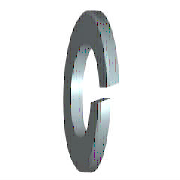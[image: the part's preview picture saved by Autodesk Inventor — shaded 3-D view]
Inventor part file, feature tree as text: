
AUTODESK INVENTOR PART (.ipt)
format: ipt  version: 2024 (Build 280153000, 153)  size: 125,440 bytes
history: native  units: mm (DEFAULTED — no unit token found)
features: extrude x2, other x1, plane x1
ambient origin geometry x6: Origin, YZ Plane, X Axis, Y Axis, Z Axis, Center Point
bodies: Solid1 (feature_tree)
feature tree (4):
  extrude  "Базовый элемент"  Depth=5.4mm
  extrude  "Вырез"  Depth=9.2mm
  other  "Work Axis1"
  plane  "Work Plane1"
